# Revit family: KEUCO_14967010000
name_source: partatom
category: Allgemeines Modell
revit_build: Autodesk Revit 2016 (Build: 20150220_1215(x64)
units: mm (PartAtom-declared; Revit-internal decimal feet)

## family parameters
Arbeitsebenenbasiert = Ja
Beim Laden mit Abzugskörper schneiden = Nein
Bemaßung runder Anschluss = Durchmesser verwenden
Gemeinsam genutzt = Nein
Immer vertikal = Nein
Kann Basisbauteil für Bewehrung sein = Nein
Raumberechnungspunkt = Nein
Teiletyp = Normal

## types (3) — shared parameters
Beschreibung = Symbol Herren
Gewicht = 2.718
Hersteller = KEUCO
Kategorie = ACC
Rail Length = 851 mm  [stored 2.79199 ft]
Serie = Plan
URL = https://www.keuco.com
Verwendung = ZU
Vorgabe-Ansicht = 1219 mm

## per-type parameters (varying)
| type | Ausschreibungstext | Material |
| 14967010000 | KEUCO PLAN Türschild 14967010000 Herren
Hochglanzverchromtes Türschild 
mit dem Symbol HERREN in quadratischer Form, 
mit abgerundeten Ecken
Maße 100 x 100 mm | Verchromt |
| 14967070000 | KEUCO PLAN Türschild 14967070000 Herren
Türschild aus hochwertigem Edelsathl 
mit dem Symbol HERREN in quadratischer Form, 
mit abgerundeten Ecken
Maße 100 x 100 mm | Edelstahl |
| 14967170000 | KEUCO PLAN Türschild 14967170000 Herren
Türschild aus silber-eloxiertem Aluminium (E6 EV1) 
mit dem Symbol HERREN in quadratischer Form, 
mit abgerundeten Ecken, 
Maße 100 x 100 mm | Verchromt |

note: column(s) folded — value = type name in every type: Artikelnummer

note: [stored X ft] marks values corroborated as IEEE doubles in the binary element streams (Revit-internal decimal feet)

## geometry (parser evidence)
native form markers: Sweep x3
no freeform markers — native parametric forms only
